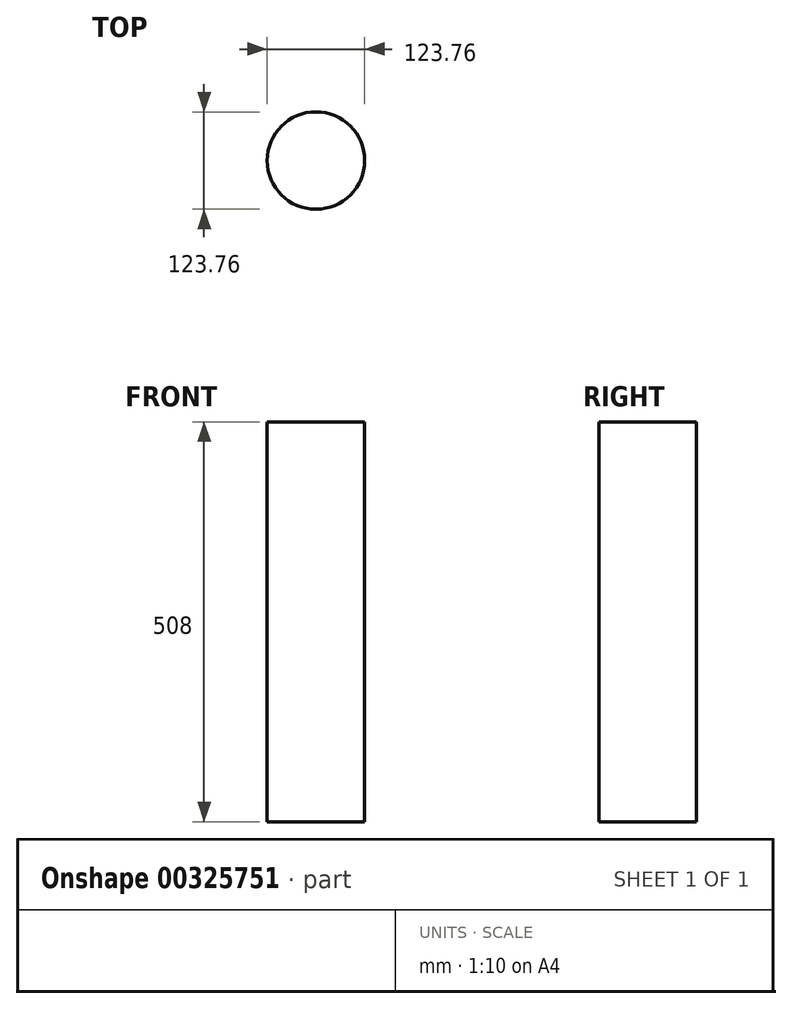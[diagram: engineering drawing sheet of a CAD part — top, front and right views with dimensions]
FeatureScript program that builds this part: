
annotation { "Feature Type Name" : "Feature", "Feature Type Description" : "" }
export const myFeature = defineFeature(function(context is Context, id is Id, definition is map)
    precondition{}
    {
        {
            var Q0;
            Q0=qCreatedBy(makeId("Top.planeOp"),FACE);
            var sketch = newSketch(context, id + "F0", { "sketchPlane" : qUnion([Q0])});
            skCircle(sketch, "E0", {"center": v(0, 0) * mm, "radius": 61.88 * mm});
            skSolve(sketch);
        }
        {
            var Q0;
            Q0=makeQuery(id+"F0.imprint","IMPRINT",FACE,{"disambiguationData":[TD([[makeQuery(id+"F0.imprint","IMPRINT",EDGE,{"derivedFrom":sQuery(id+"F0.wireOp",EDGE,"E0")}),1.0]])]});
            extrude(context, id + "F1", {"entities" : qUnion([Q0]), "depth" : 508 * mm});
        }
    });
